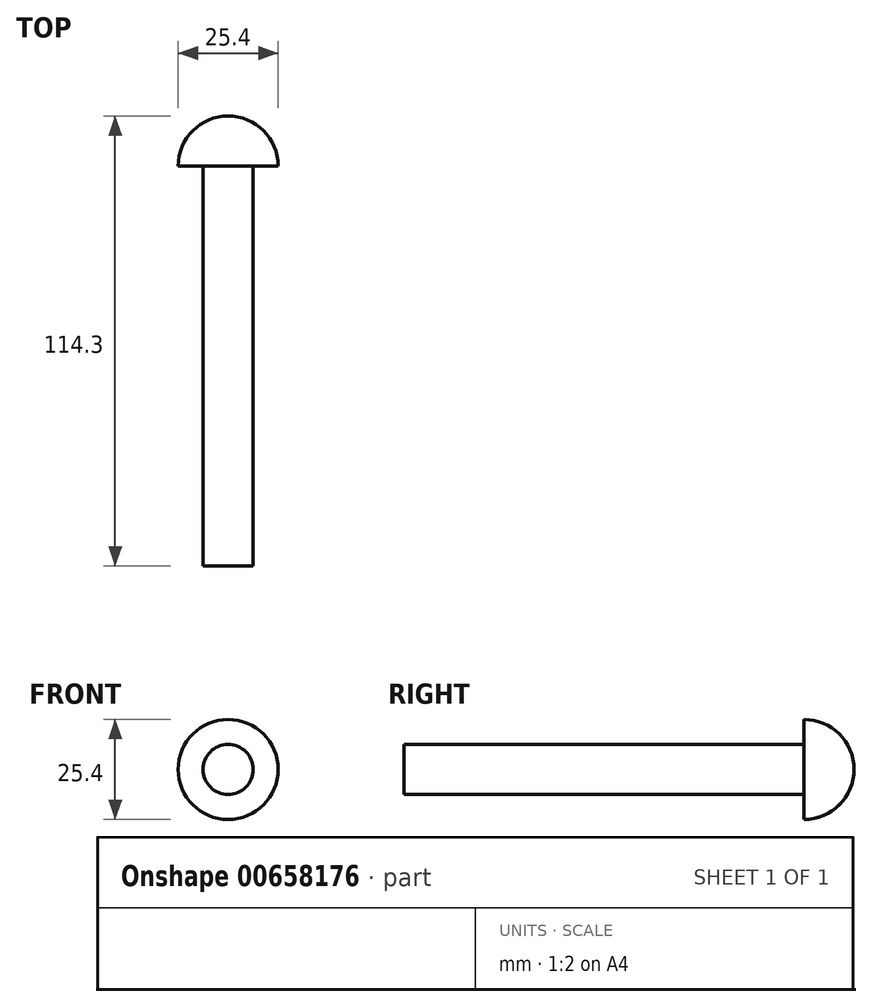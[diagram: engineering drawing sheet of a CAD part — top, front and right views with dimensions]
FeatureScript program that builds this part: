
annotation { "Feature Type Name" : "Feature", "Feature Type Description" : "" }
export const myFeature = defineFeature(function(context is Context, id is Id, definition is map)
    precondition{}
    {
        {
            var Q0;
            Q0=qCreatedBy(makeId("Front.planeOp"),FACE);
            var sketch = newSketch(context, id + "F0", { "sketchPlane" : qUnion([Q0])});
            skCircle(sketch, "E0", {"center": v(0, 0) * mm, "radius": 6.35 * mm});
            skSolve(sketch);
        }
        {
            var Q0;
            Q0 = qSketchRegion(id + "F0", true);
            extrude(context, id + "F1", {"entities" : qUnion([Q0]), "depth" : 101.6 * mm, "offsetDistance" : 25.4 * mm});
        }
        {
            var Q0;
            Q0=qCreatedBy(makeId("Right.planeOp"),FACE);
            var sketch = newSketch(context, id + "F2", { "sketchPlane" : qUnion([Q0])});
            skLineSegment(sketch, "E1", {"start": v(12.7, 0) * mm, "end": v(0, 0) * mm});
            skLineSegment(sketch, "E2", {"start": v(0, 0) * mm, "end": v(0, 12.7) * mm});
            skArc(sketch, "E3", {"start": v(0, 12.7) * mm, "mid": v(8.98, 8.98) * mm, "end": v(12.7, 0) * mm});
            skSolve(sketch);
        }
        {
            var Q0;
            Q0=makeQuery(id+"F2.imprint","IMPRINT",FACE,{"disambiguationData":[TD([[makeQuery(id+"F2.imprint","IMPRINT",EDGE,{"derivedFrom":sQuery(id+"F2.wireOp",EDGE,"E1")}),-1.0]])]});
            var Q1;
            Q1=sQuery(id+"F2.wireOp",EDGE,"E1");
            var Q2;
            Q2=sQuery(id+"F2.wireOp",EDGE,"E3");
            var Q3;
            Q3=sQuery(id+"F2.wireOp",EDGE,"E2");
            var Q4;
            Q4=sQuery(id+"F2.wireOp",EDGE,"E1");
            revolve(context, id + "F3", {"operationType" : NewBodyOperationType.ADD, "entities" : qUnion([Q0]), "surfaceEntities" : qUnion([Q1, Q2, Q3]), "axis" : qUnion([Q4]), "revolveType" : RevolveType.FULL});
        }
    });
